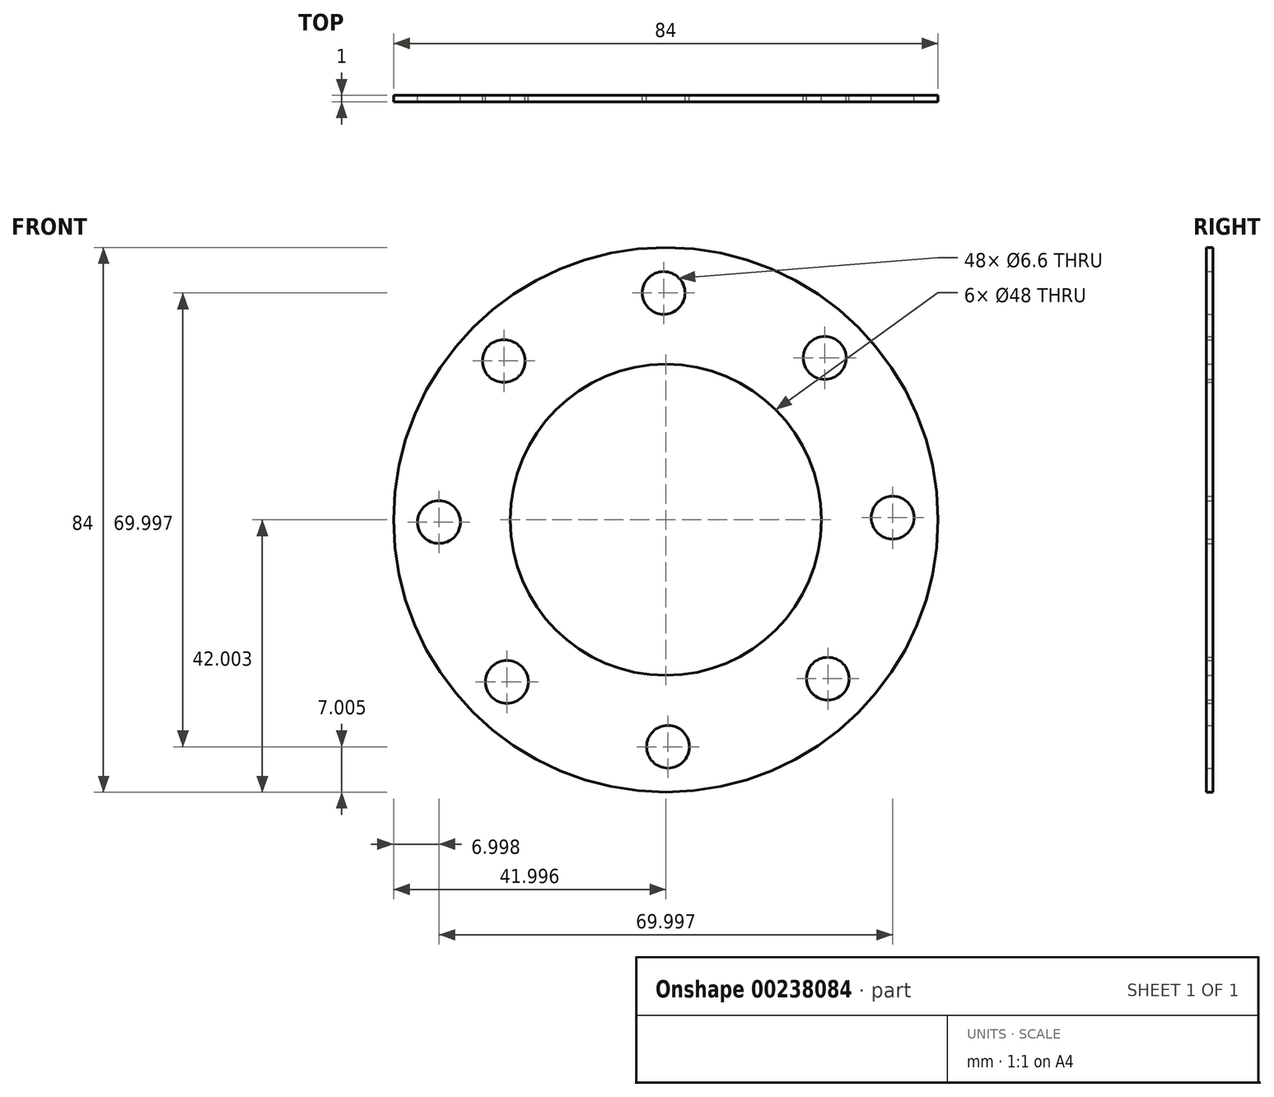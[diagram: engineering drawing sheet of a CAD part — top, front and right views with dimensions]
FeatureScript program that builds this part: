
annotation { "Feature Type Name" : "Feature", "Feature Type Description" : "" }
export const myFeature = defineFeature(function(context is Context, id is Id, definition is map)
    precondition{}
    {
        {
            var Q0;
            Q0=qCreatedBy(makeId("Front.planeOp"),FACE);
            var sketch = newSketch(context, id + "F0", { "sketchPlane" : qUnion([Q0])});
            skCircle(sketch, "E0", {"center": v(-2.96, 0.5) * mm, "radius": 42 * mm});
            skCircle(sketch, "E1", {"center": v(-2.96, 0.5) * mm, "radius": 24 * mm});
            skCircle(sketch, "E2", {"center": v(-2.96, 0.5) * mm, "radius": 35 * mm});
            skCircle(sketch, "E3", {"center": v(-3.3, 35.5) * mm, "radius": 3.3 * mm});
            skCircle(sketch, "E4.1.0", {"center": v(-27.95, 25) * mm, "radius": 3.3 * mm});
            skCircle(sketch, "E4.2.0", {"center": v(-37.96, 0.15) * mm, "radius": 3.3 * mm});
            skCircle(sketch, "E4.3.0", {"center": v(-27.47, -24.5) * mm, "radius": 3.3 * mm});
            skCircle(sketch, "E4.4.0", {"center": v(-2.62, -34.5) * mm, "radius": 3.3 * mm});
            skCircle(sketch, "E4.5.0", {"center": v(22.02, -24.01) * mm, "radius": 3.3 * mm});
            skCircle(sketch, "E4.6.0", {"center": v(32.03, 0.83) * mm, "radius": 3.3 * mm});
            skCircle(sketch, "E4.7.0", {"center": v(21.54, 25.48) * mm, "radius": 3.3 * mm});
            skSolve(sketch);
        }
        {
            var Q0;
            Q0=makeQuery(id+"F0.imprint","IMPRINT",FACE,{"disambiguationData":[TD([[makeQuery(id+"F0.imprint","IMPRINT",EDGE,{"derivedFrom":sQuery(id+"F0.wireOp",EDGE,"E1")}),-1.0]])]});
            var Q1;
            Q1=makeQuery(id+"F0.imprint","IMPRINT",FACE,{"disambiguationData":[TD([[makeQuery(id+"F0.imprint","IMPRINT",EDGE,{"derivedFrom":sQuery(id+"F0.wireOp",EDGE,"E0")}),1.0]])]});
            extrude(context, id + "F1", {"entities" : qUnion([Q0, Q1]), "depth" : 1 * mm});
        }
    });
